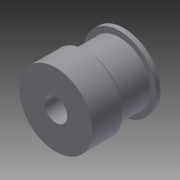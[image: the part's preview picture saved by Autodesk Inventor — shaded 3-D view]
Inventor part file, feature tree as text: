
AUTODESK INVENTOR PART (.ipt)
format: ipt  version: 2013 (Build 170138000, 138)  size: 104,448 bytes
history: native  units: mm
features: revolve x1, sketch x1
ambient origin geometry x8: Origin, YZ Plane, XZ Plane, XY Plane, X Axis, Y Axis, Z Axis, Center Point
feature tree (2):
  revolve  "Revolution2"  [1 undecoded]
  sketch  "Sketch1"  dims[d0=5.5mm d1=7.0mm d2=7.0mm d4=2.5mm d5=90.0deg d6=15.0mm d7=4.25mm d8=0.4mm d9=0.4mm]
note: 1 required parameter value undecoded (feature->parameter linkage not recoverable at this tier; creation-order binding heuristic only, values carry confidence <= 0.55)
